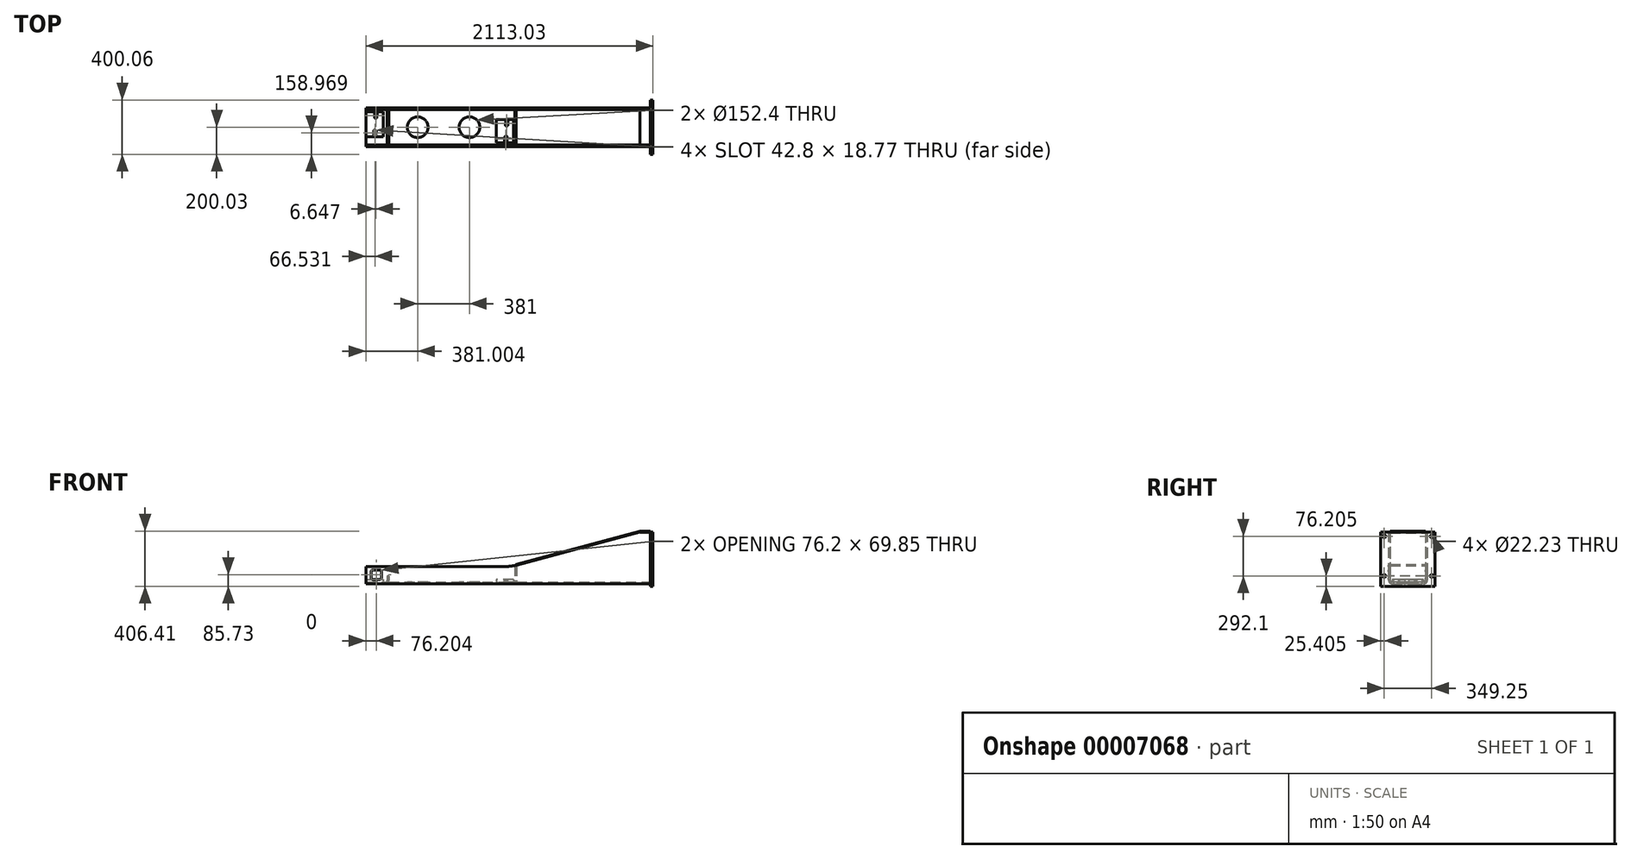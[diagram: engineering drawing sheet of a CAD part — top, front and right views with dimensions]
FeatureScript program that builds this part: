
annotation { "Feature Type Name" : "Feature", "Feature Type Description" : "" }
export const myFeature = defineFeature(function(context is Context, id is Id, definition is map)
    precondition{}
    {
        {
            var Q0;
            Q0=qCreatedBy(makeId("Right.planeOp"),FACE);
            var sketch = newSketch(context, id + "F0", { "sketchPlane" : qUnion([Q0])});
            skLineSegment(sketch, "E0.rect.bottom", {"start": v(-200.02, 200.03) * mm, "end": v(200.03, 200.03) * mm});
            skLineSegment(sketch, "E0.rect.top", {"start": v(-200.03, -200.03) * mm, "end": v(200.02, -200.03) * mm});
            skLineSegment(sketch, "E0.rect.left", {"start": v(-200.02, 200.03) * mm, "end": v(-200.03, -200.03) * mm});
            skLineSegment(sketch, "E0.rect.right", {"start": v(200.03, 200.03) * mm, "end": v(200.02, -200.03) * mm});
            skPoint(sketch, "E0.rect.middle", {"position": v(0, 0) * mm});
            skLineSegment(sketch, "E1.0", {"start": v(-200.03, -123.83) * mm, "end": v(200.02, -123.83) * mm, "construction": true});
            skLineSegment(sketch, "E2.0", {"start": v(-200.03, 168.28) * mm, "end": v(200.02, 168.28) * mm, "construction": true});
            skLineSegment(sketch, "E3", {"start": v(0, 200.03) * mm, "end": v(0, -200.03) * mm, "construction": true});
            skLineSegment(sketch, "E4.0", {"start": v(-174.62, 200.03) * mm, "end": v(-174.63, -200.02) * mm, "construction": true});
            skCircle(sketch, "E5", {"center": v(-174.62, 168.28) * mm, "radius": 11.11 * mm});
            skCircle(sketch, "E6", {"center": v(-174.63, -123.83) * mm, "radius": 11.11 * mm});
            skCircle(sketch, "E7.0.MirrorC", {"center": v(174.63, 168.27) * mm, "radius": 11.11 * mm});
            skCircle(sketch, "E8.0.MirrorC", {"center": v(174.62, -123.83) * mm, "radius": 11.11 * mm});
            skSolve(sketch);
        }
        {
            var Q0;
            Q0 = qSketchRegion(id + "F0", true);
            extrude(context, id + "F1", {"entities" : qUnion([Q0]), "depth" : 19.05 * mm});
        }
        {
            var Q0;
            Q0=makeQuery(id+"F1.opExtrude","CAP_FACE",FACE,{"disambiguationData":[OSD([sQuery(id+"F0.wireOp",EDGE,"E0.rect.bottom"),sQuery(id+"F0.wireOp",EDGE,"E0.rect.top"),sQuery(id+"F0.wireOp",EDGE,"E0.rect.left"),sQuery(id+"F0.wireOp",EDGE,"E0.rect.right"),sQuery(id+"F0.wireOp",EDGE,"E5"),sQuery(id+"F0.wireOp",EDGE,"E6"),sQuery(id+"F0.wireOp",EDGE,"E7.0.MirrorC"),sQuery(id+"F0.wireOp",EDGE,"E8.0.MirrorC")])],"isStart":true});
            var sketch = newSketch(context, id + "F2", { "sketchPlane" : qUnion([Q0])});
            skLineSegment(sketch, "E9", {"start": v(0, 200.03) * mm, "end": v(0, -200.03) * mm, "construction": true});
            skLineSegment(sketch, "E10.0", {"start": v(0, -180.97) * mm, "end": v(-117.47, -180.97) * mm});
            skLineSegment(sketch, "E11.0", {"start": v(0, -168.28) * mm, "end": v(-117.47, -168.28) * mm});
            skLineSegment(sketch, "E12.0", {"start": v(-130.18, 200.02) * mm, "end": v(-130.17, -155.58) * mm});
            skLineSegment(sketch, "E13.0", {"start": v(-142.88, 200.02) * mm, "end": v(-142.87, -155.57) * mm});
            skArc(sketch, "E14.filletArc", {"start": v(-130.17, -155.58) * mm, "mid": v(-126.46, -164.56) * mm, "end": v(-117.47, -168.28) * mm});
            skArc(sketch, "E15.filletArc", {"start": v(-142.87, -155.57) * mm, "mid": v(-135.44, -173.54) * mm, "end": v(-117.47, -180.97) * mm});
            skLineSegment(sketch, "E16", {"start": v(-142.88, 200.02) * mm, "end": v(-130.18, 200.02) * mm});
            skLineSegment(sketch, "E17.0.MirrorCS", {"start": v(142.87, 200.03) * mm, "end": v(130.17, 200.03) * mm});
            skArc(sketch, "E17.1.MirrorCS", {"start": v(130.18, -155.57) * mm, "mid": v(126.46, -164.56) * mm, "end": v(117.48, -168.27) * mm});
            skLineSegment(sketch, "E17.2.MirrorCS", {"start": v(0, -180.97) * mm, "end": v(117.48, -180.97) * mm});
            skLineSegment(sketch, "E17.3.MirrorCS", {"start": v(130.17, 200.03) * mm, "end": v(130.18, -155.57) * mm});
            skLineSegment(sketch, "E17.4.MirrorCS", {"start": v(0, -168.28) * mm, "end": v(117.48, -168.27) * mm});
            skLineSegment(sketch, "E17.5.MirrorCS", {"start": v(142.87, 200.03) * mm, "end": v(142.88, -155.57) * mm});
            skArc(sketch, "E17.6.MirrorCS", {"start": v(142.88, -155.57) * mm, "mid": v(135.44, -173.54) * mm, "end": v(117.48, -180.97) * mm});
            skSolve(sketch);
        }
        {
            var Q0;
            Q0 = qSketchRegion(id + "F2", true);
            extrude(context, id + "F3", {"entities" : qUnion([Q0]), "operationType" : NewBodyOperationType.ADD, "depth" : 2093.98 * mm});
        }
        {
            var Q0;
            Q0=makeQuery(id+"F3.opExtrude","SWEPT_FACE",FACE,{"disambiguationData":[OSD([sQuery(id+"F2.wireOp",EDGE,"E17.5.MirrorCS")])]});
            var sketch = newSketch(context, id + "F4", { "sketchPlane" : qUnion([Q0])});
            skLineSegment(sketch, "E18.0", {"start": v(-76.2, 200.02) * mm, "end": v(-76.2, -200.03) * mm, "construction": true});
            skLineSegment(sketch, "E19.0", {"start": v(-2093.98, -53.97) * mm, "end": v(-1064.27, -53.97) * mm});
            skLineSegment(sketch, "E20", {"start": v(-76.2, 200.02) * mm, "end": v(-985.38, -43.59) * mm});
            skLineSegment(sketch, "E21", {"start": v(-89.08, 249.31) * mm, "end": v(-1474.33, 249.31) * mm, "construction": true});
            skArc(sketch, "E22.filletArc", {"start": v(-1064.27, -53.97) * mm, "mid": v(-1024.48, -51.37) * mm, "end": v(-985.38, -43.59) * mm});
            skLineSegment(sketch, "E23", {"start": v(-76.2, 200.02) * mm, "end": v(-76.2, 325.81) * mm});
            skLineSegment(sketch, "E24", {"start": v(-76.2, 325.81) * mm, "end": v(-2093.98, 325.81) * mm});
            skLineSegment(sketch, "E25", {"start": v(-2093.98, 325.81) * mm, "end": v(-2093.98, -53.97) * mm});
            skSolve(sketch);
        }
        {
            var Q0;
            Q0 = qSketchRegion(id + "F4", true);
            extrude(context, id + "F5", {"entities" : qUnion([Q0]), "operationType" : NewBodyOperationType.REMOVE, "endBound" : BoundingType.THROUGH_ALL, "oppositeDirection" : true, "depth" : 25.4 * mm});
        }
        {
            var Q0;
            Q0=makeQuery(id+"F3.opExtrude","SWEPT_FACE",FACE,{"disambiguationData":[OSD([sQuery(id+"F2.wireOp",EDGE,"E12.0")])]});
            var sketch = newSketch(context, id + "F6", { "sketchPlane" : qUnion([Q0])});
            skLineSegment(sketch, "E26.0", {"start": v(-76.25, 200.21) * mm, "end": v(-985.43, -43.4) * mm});
            skSolve(sketch);
        }
        {
            var Q0;
            {var subQ0=sQuery(id+"F2.wireOp",EDGE,"E12.0");Q0=makeQuery(id+"F6.imprint","IMPRINT",FACE,{"disambiguationData":[TD([[makeQuery(id+"F6.imprint","IMPRINT",EDGE,{"derivedFrom":makeQuery(id+"F3.opExtrude","CAP_EDGE",EDGE,{"disambiguationData":[OSD([subQ0])],"isStart":true})}),-1.0]])]});}
            var sketch = newSketch(context, id + "F7", { "sketchPlane" : qUnion([Q0])});
            skLineSegment(sketch, "E27.0", {"start": v(-74.6, 194.08) * mm, "end": v(-983.79, -49.53) * mm});
            skLineSegment(sketch, "E28.0", {"start": v(-77.9, 206.35) * mm, "end": v(-987.07, -37.27) * mm});
            skLineSegment(sketch, "E29.0", {"start": v(-76.2, 193.68) * mm, "end": v(0, 193.68) * mm});
            skLineSegment(sketch, "E30.0", {"start": v(-76.2, 206.38) * mm, "end": v(0, 206.38) * mm});
            skLineSegment(sketch, "E31", {"start": v(-76.2, 206.38) * mm, "end": v(-76.2, 193.68) * mm});
            skLineSegment(sketch, "E32", {"start": v(-74.6, 194.08) * mm, "end": v(-77.9, 206.35) * mm});
            skLineSegment(sketch, "E33", {"start": v(0, 206.38) * mm, "end": v(0, 193.68) * mm});
            skLineSegment(sketch, "E34", {"start": v(-987.07, -37.27) * mm, "end": v(-983.79, -49.53) * mm});
            skSolve(sketch);
        }
        {
            var Q0;
            Q0 = qSketchRegion(id + "F7", true);
            extrude(context, id + "F8", {"entities" : qUnion([Q0]), "operationType" : NewBodyOperationType.ADD, "depth" : 260.35 * mm});
        }
        {
            var Q0;
            Q0=qCreatedBy(makeId("Right.planeOp"),FACE);
            cPlane(context, id + "F9", {"entities" : qUnion([Q0]), "cplaneType" : CPlaneType.OFFSET, "offset" : 984.25 * mm, "oppositeDirection" : true, "width" : 152.4 * mm, "height" : 152.4 * mm});
        }
        {
            var Q0;
            Q0=qCreatedBy(id+"F9.planeOp",FACE);
            var sketch = newSketch(context, id + "F10", { "sketchPlane" : qUnion([Q0])});
            skLineSegment(sketch, "E35.0", {"start": v(-130.18, -49.53) * mm, "end": v(130.17, -49.53) * mm});
            skLineSegment(sketch, "E36.0", {"start": v(130.17, -49.53) * mm, "end": v(130.17, -155.58) * mm});
            skArc(sketch, "E37.0", {"start": v(130.17, -155.58) * mm, "mid": v(126.46, -164.56) * mm, "end": v(117.47, -168.28) * mm});
            skLineSegment(sketch, "E38.0", {"start": v(117.47, -168.28) * mm, "end": v(-117.48, -168.27) * mm});
            skArc(sketch, "E39.0", {"start": v(-130.18, -155.57) * mm, "mid": v(-126.46, -164.56) * mm, "end": v(-117.48, -168.27) * mm});
            skLineSegment(sketch, "E40.0", {"start": v(-130.18, -49.53) * mm, "end": v(-130.18, -155.57) * mm});
            skPoint(sketch, "E41.orphan", {"position": v(130.17, -53.97) * mm});
            skPoint(sketch, "E42.orphan", {"position": v(-130.18, -53.97) * mm});
            skSolve(sketch);
        }
        {
            var Q0;
            Q0 = qSketchRegion(id + "F10", true);
            extrude(context, id + "F11", {"entities" : qUnion([Q0]), "operationType" : NewBodyOperationType.ADD, "oppositeDirection" : true, "depth" : 12.7 * mm});
        }
        {
            var Q0;
            {var subQ0=sQuery(id+"F2.wireOp",EDGE,"E11.0");var subQ1=sQuery(id+"F2.wireOp",EDGE,"E17.4.MirrorCS");Q0=makeQuery(id+"F11.boolean.opBoolean","SPLIT",FACE,{"disambiguationData":[TD([makeQuery(id+"F11.opExtrude","CAP_FACE",FACE,{"disambiguationData":[OSD([sQuery(id+"F10.wireOp",EDGE,"E35.0"),sQuery(id+"F10.wireOp",EDGE,"E36.0"),sQuery(id+"F10.wireOp",EDGE,"E37.0"),sQuery(id+"F10.wireOp",EDGE,"E38.0"),sQuery(id+"F10.wireOp",EDGE,"E39.0"),sQuery(id+"F10.wireOp",EDGE,"E40.0")])],"isStart":false})])],"derivedFrom":makeQuery(id+"F3.opExtrude","SWEPT_FACE",FACE,{"disambiguationData":[OSD([subQ0,subQ1])]})});}
            var sketch = newSketch(context, id + "F12", { "sketchPlane" : qUnion([Q0])});
            skLineSegment(sketch, "E43.0", {"start": v(-2093.98, 117.47) * mm, "end": v(-2093.98, -117.48) * mm, "construction": true});
            skLineSegment(sketch, "E44", {"start": v(-2093.98, 0) * mm, "end": v(-1025.05, 0) * mm, "construction": true});
            skLineSegment(sketch, "E45.0", {"start": v(-1712.98, 117.47) * mm, "end": v(-1712.98, -117.48) * mm, "construction": true});
            skLineSegment(sketch, "E46.0", {"start": v(-1331.98, 117.47) * mm, "end": v(-1331.98, -117.48) * mm, "construction": true});
            skCircle(sketch, "E47", {"center": v(-1712.98, 0) * mm, "radius": 76.2 * mm});
            skCircle(sketch, "E48", {"center": v(-1331.98, 0) * mm, "radius": 76.2 * mm});
            skSolve(sketch);
        }
        {
            var Q0;
            Q0 = qSketchRegion(id + "F12", true);
            extrude(context, id + "F13", {"entities" : qUnion([Q0]), "operationType" : NewBodyOperationType.REMOVE, "endBound" : BoundingType.THROUGH_ALL, "oppositeDirection" : true, "depth" : 25.4 * mm});
        }
        {
            var Q0;
            Q0=makeQuery(id+"F3.opExtrude","SWEPT_FACE",FACE,{"disambiguationData":[OSD([sQuery(id+"F2.wireOp",EDGE,"E17.5.MirrorCS")])]});
            var sketch = newSketch(context, id + "F14", { "sketchPlane" : qUnion([Q0])});
            skLineSegment(sketch, "E49.0", {"start": v(-2043.18, -149.22) * mm, "end": v(-1992.38, -149.22) * mm});
            skLineSegment(sketch, "E50.0", {"start": v(-2043.18, -79.37) * mm, "end": v(-1992.38, -79.37) * mm});
            skLineSegment(sketch, "E51.0", {"start": v(-2055.88, -92.07) * mm, "end": v(-2055.88, -136.53) * mm});
            skLineSegment(sketch, "E52.0", {"start": v(-1979.68, -92.07) * mm, "end": v(-1979.68, -136.52) * mm});
            skPoint(sketch, "E53.visualSharp", {"position": v(-2055.88, -79.37) * mm});
            skArc(sketch, "E53.filletArc", {"start": v(-2043.18, -79.37) * mm, "mid": v(-2052.16, -83.1) * mm, "end": v(-2055.88, -92.07) * mm});
            skPoint(sketch, "E54.visualSharp", {"position": v(-1979.68, -79.37) * mm});
            skArc(sketch, "E54.filletArc", {"start": v(-1979.68, -92.07) * mm, "mid": v(-1983.4, -83.1) * mm, "end": v(-1992.38, -79.37) * mm});
            skPoint(sketch, "E55.visualSharp", {"position": v(-1979.68, -149.22) * mm});
            skArc(sketch, "E55.filletArc", {"start": v(-1992.38, -149.22) * mm, "mid": v(-1983.4, -145.5) * mm, "end": v(-1979.68, -136.52) * mm});
            skPoint(sketch, "E56.visualSharp", {"position": v(-2055.88, -149.22) * mm});
            skArc(sketch, "E56.filletArc", {"start": v(-2055.88, -136.53) * mm, "mid": v(-2052.16, -145.5) * mm, "end": v(-2043.18, -149.23) * mm});
            skSolve(sketch);
        }
        {
            var Q0;
            Q0 = qSketchRegion(id + "F14", true);
            extrude(context, id + "F15", {"entities" : qUnion([Q0]), "operationType" : NewBodyOperationType.REMOVE, "endBound" : BoundingType.THROUGH_ALL, "oppositeDirection" : true, "depth" : 25.4 * mm});
        }
        {
            var Q0;
            Q0=makeQuery(id+"F11.opExtrude","CAP_FACE",FACE,{"disambiguationData":[OSD([sQuery(id+"F10.wireOp",EDGE,"E35.0"),sQuery(id+"F10.wireOp",EDGE,"E36.0"),sQuery(id+"F10.wireOp",EDGE,"E37.0"),sQuery(id+"F10.wireOp",EDGE,"E38.0"),sQuery(id+"F10.wireOp",EDGE,"E39.0"),sQuery(id+"F10.wireOp",EDGE,"E40.0")])],"isStart":false});
            cPlane(context, id + "F16", {"entities" : qUnion([Q0]), "cplaneType" : CPlaneType.OFFSET, "offset" : 939.8 * mm, "width" : 152.4 * mm, "height" : 152.4 * mm});
        }
        {
            var Q0;
            Q0=qCreatedBy(id+"F16.planeOp",FACE);
            var sketch = newSketch(context, id + "F17", { "sketchPlane" : qUnion([Q0])});
            skLineSegment(sketch, "E57.0", {"start": v(-130.17, -123.83) * mm, "end": v(-130.17, -155.58) * mm});
            skArc(sketch, "E58.0", {"start": v(-130.17, -155.58) * mm, "mid": v(-126.46, -164.56) * mm, "end": v(-117.47, -168.28) * mm});
            skLineSegment(sketch, "E59.0", {"start": v(-117.47, -168.28) * mm, "end": v(117.48, -168.27) * mm});
            skArc(sketch, "E60.0", {"start": v(130.18, -155.57) * mm, "mid": v(126.46, -164.56) * mm, "end": v(117.48, -168.27) * mm});
            skLineSegment(sketch, "E61.0", {"start": v(130.18, -123.82) * mm, "end": v(130.18, -155.57) * mm});
            skLineSegment(sketch, "E62.0", {"start": v(-130.17, -123.83) * mm, "end": v(130.18, -123.82) * mm});
            skPoint(sketch, "E63.orphan", {"position": v(-130.17, -53.97) * mm});
            skPoint(sketch, "E64.orphan", {"position": v(130.18, -53.97) * mm});
            skSolve(sketch);
        }
        {
            var Q0;
            Q0 = qSketchRegion(id + "F17", true);
            extrude(context, id + "F18", {"entities" : qUnion([Q0]), "operationType" : NewBodyOperationType.ADD, "oppositeDirection" : true, "depth" : 12.7 * mm});
        }
        {
            var Q0;
            {var subQ0=sQuery(id+"F2.wireOp",EDGE,"E11.0");var subQ1=sQuery(id+"F2.wireOp",EDGE,"E17.4.MirrorCS");Q0=makeQuery(id+"F18.boolean.opBoolean","SPLIT",FACE,{"disambiguationData":[TD([makeQuery(id+"F18.opExtrude","CAP_FACE",FACE,{"disambiguationData":[OSD([sQuery(id+"F17.wireOp",EDGE,"E57.0"),sQuery(id+"F17.wireOp",EDGE,"E58.0"),sQuery(id+"F17.wireOp",EDGE,"E59.0"),sQuery(id+"F17.wireOp",EDGE,"E60.0"),sQuery(id+"F17.wireOp",EDGE,"E61.0"),sQuery(id+"F17.wireOp",EDGE,"E62.0")])],"isStart":true})])],"derivedFrom":makeQuery(id+"F11.boolean.opBoolean","SPLIT",FACE,{"disambiguationData":[TD([makeQuery(id+"F11.opExtrude","CAP_FACE",FACE,{"disambiguationData":[OSD([sQuery(id+"F10.wireOp",EDGE,"E35.0"),sQuery(id+"F10.wireOp",EDGE,"E36.0"),sQuery(id+"F10.wireOp",EDGE,"E37.0"),sQuery(id+"F10.wireOp",EDGE,"E38.0"),sQuery(id+"F10.wireOp",EDGE,"E39.0"),sQuery(id+"F10.wireOp",EDGE,"E40.0")])],"isStart":false})])],"derivedFrom":makeQuery(id+"F3.opExtrude","SWEPT_FACE",FACE,{"disambiguationData":[OSD([subQ0,subQ1])]})})});}
            var sketch = newSketch(context, id + "F19", { "sketchPlane" : qUnion([Q0])});
            skLineSegment(sketch, "E65.0", {"start": v(-2093.98, 114.3) * mm, "end": v(-2093.98, -69.85) * mm});
            skLineSegment(sketch, "E66.0", {"start": v(-1966.98, 114.3) * mm, "end": v(-1966.98, -69.85) * mm});
            skLineSegment(sketch, "E67", {"start": v(-2093.98, 0) * mm, "end": v(-1966.98, 0) * mm, "construction": true});
            skLineSegment(sketch, "E68.0", {"start": v(-2093.98, -69.85) * mm, "end": v(-1966.98, -69.85) * mm});
            skLineSegment(sketch, "E69.0", {"start": v(-2093.98, 114.3) * mm, "end": v(-1966.98, 114.3) * mm});
            skPoint(sketch, "E70.orphan", {"position": v(-1966.98, 117.47) * mm});
            skPoint(sketch, "E71.orphan", {"position": v(-2093.98, 117.47) * mm});
            skPoint(sketch, "E72.orphan", {"position": v(-1966.98, -117.48) * mm});
            skPoint(sketch, "E73.orphan", {"position": v(-2093.98, -117.48) * mm});
            skSolve(sketch);
        }
        {
            var Q0;
            Q0 = qSketchRegion(id + "F19", true);
            extrude(context, id + "F20", {"entities" : qUnion([Q0]), "operationType" : NewBodyOperationType.ADD, "depth" : 19.05 * mm});
        }
        {
            var Q0;
            {var subQ0=sQuery(id+"F2.wireOp",EDGE,"E11.0");var subQ1=sQuery(id+"F2.wireOp",EDGE,"E17.4.MirrorCS");var subQ6=makeQuery(id+"F11.opExtrude","CAP_FACE",FACE,{"disambiguationData":[OSD([sQuery(id+"F10.wireOp",EDGE,"E35.0"),sQuery(id+"F10.wireOp",EDGE,"E36.0"),sQuery(id+"F10.wireOp",EDGE,"E37.0"),sQuery(id+"F10.wireOp",EDGE,"E38.0"),sQuery(id+"F10.wireOp",EDGE,"E39.0"),sQuery(id+"F10.wireOp",EDGE,"E40.0")])],"isStart":false});Q0=makeQuery(id+"F18.boolean.opBoolean","SPLIT",FACE,{"disambiguationData":[TD([makeQuery(id+"F13.boolean.opBoolean","COPY",FACE,{"derivedFrom":makeQuery(id+"F13.opExtrude","SWEPT_FACE",FACE,{"disambiguationData":[OSD([sQuery(id+"F12.wireOp",EDGE,"E47")])]})})])],"derivedFrom":makeQuery(id+"F11.boolean.opBoolean","SPLIT",FACE,{"disambiguationData":[TD([subQ6])],"derivedFrom":makeQuery(id+"F3.opExtrude","SWEPT_FACE",FACE,{"disambiguationData":[OSD([subQ0,subQ1])]})})});}
            var sketch = newSketch(context, id + "F21", { "sketchPlane" : qUnion([Q0])});
            skLineSegment(sketch, "E74", {"start": v(-996.95, 0) * mm, "end": v(-2205.84, 0) * mm, "construction": true});
            skLineSegment(sketch, "E75.0", {"start": v(-1135.13, 57.15) * mm, "end": v(-1135.13, -114.3) * mm});
            skLineSegment(sketch, "E76.0", {"start": v(-1008.13, 57.15) * mm, "end": v(-1008.13, -114.3) * mm});
            skLineSegment(sketch, "E77.0", {"start": v(-1008.13, -114.3) * mm, "end": v(-1135.13, -114.3) * mm});
            skLineSegment(sketch, "E78.0", {"start": v(-1008.13, 57.15) * mm, "end": v(-1135.13, 57.15) * mm});
            skSolve(sketch);
        }
        {
            var Q0;
            Q0 = qSketchRegion(id + "F21", true);
            extrude(context, id + "F22", {"entities" : qUnion([Q0]), "operationType" : NewBodyOperationType.ADD, "depth" : 19.05 * mm});
        }
        {
            var Q0;
            Q0=makeQuery(id+"F22.opExtrude","CAP_FACE",FACE,{"disambiguationData":[OSD([sQuery(id+"F21.wireOp",EDGE,"E75.0"),sQuery(id+"F21.wireOp",EDGE,"E76.0"),sQuery(id+"F21.wireOp",EDGE,"E77.0"),sQuery(id+"F21.wireOp",EDGE,"E78.0")])],"isStart":false});
            var sketch = newSketch(context, id + "F23", { "sketchPlane" : qUnion([Q0])});
            skLineSegment(sketch, "E79", {"start": v(110.37, 0) * mm, "end": v(-2176.16, 0) * mm, "construction": true});
            skLineSegment(sketch, "E80.0", {"start": v(110.37, 22.35) * mm, "end": v(-2176.16, 22.35) * mm, "construction": true});
            skLineSegment(sketch, "E81.0", {"start": v(110.37, -28.45) * mm, "end": v(-2176.16, -28.45) * mm, "construction": true});
            skLineSegment(sketch, "E82.0", {"start": v(-2093.98, 114.3) * mm, "end": v(-2093.98, -69.85) * mm, "construction": true});
            skLineSegment(sketch, "E83.0", {"start": v(-2024.13, 114.3) * mm, "end": v(-2024.13, -69.85) * mm, "construction": true});
            skLineSegment(sketch, "E84.0", {"start": v(-1060.45, 114.3) * mm, "end": v(-1060.45, -69.85) * mm, "construction": true});
            skLineSegment(sketch, "E85", {"start": v(-2026.79, -28.45) * mm, "end": v(-2013.86, 218.3) * mm, "construction": true});
            skLineSegment(sketch, "E86", {"start": v(-2024.13, 22.35) * mm, "end": v(-1060.45, -28.15) * mm, "construction": true});
            skLineSegment(sketch, "E87.0", {"start": v(-2020.8, 85.76) * mm, "end": v(-1880.93, 78.43) * mm, "construction": true});
            skLineSegment(sketch, "E88.0", {"start": v(-2021.47, 73.08) * mm, "end": v(-1881.6, 65.75) * mm, "construction": true});
            skLineSegment(sketch, "E89", {"start": v(-2028.86, 98.9) * mm, "end": v(-2030.19, 73.54) * mm});
            skLineSegment(sketch, "E90", {"start": v(-2011.42, 98) * mm, "end": v(-2012.75, 72.63) * mm});
            skArc(sketch, "E91.trimOffspring", {"start": v(-2028.86, 98.9) * mm, "mid": v(-2019.68, 107.17) * mm, "end": v(-2011.42, 98) * mm});
            skArc(sketch, "E92.trimOffspring", {"start": v(-2030.19, 73.54) * mm, "mid": v(-2021.92, 64.36) * mm, "end": v(-2012.75, 72.63) * mm});
            skLineSegment(sketch, "E93.0.MirrorCS", {"start": v(-2019.4, -54.2) * mm, "end": v(-2018.07, -28.84) * mm});
            skArc(sketch, "E94.0.MirrorCS", {"start": v(-2036.83, -53.29) * mm, "mid": v(-2028.57, -62.46) * mm, "end": v(-2019.4, -54.2) * mm});
            skLineSegment(sketch, "E95.0.MirrorCS", {"start": v(-2036.83, -53.29) * mm, "end": v(-2035.5, -27.92) * mm});
            skArc(sketch, "E96.0.MirrorCS", {"start": v(-2035.5, -27.92) * mm, "mid": v(-2026.33, -19.66) * mm, "end": v(-2018.07, -28.84) * mm});
            skLineSegment(sketch, "E97", {"start": v(-1542.29, -2.9) * mm, "end": v(-1531.97, 193.95) * mm, "construction": true});
            skLineSegment(sketch, "E98.0.MirrorCS", {"start": v(-1063.11, -78.95) * mm, "end": v(-1050.18, 167.8) * mm, "construction": true});
            skLineSegment(sketch, "E99.0", {"start": v(-2027.12, -34.72) * mm, "end": v(-1063.44, -85.22) * mm, "construction": true});
            skLineSegment(sketch, "E100.0", {"start": v(-2026.45, -22.04) * mm, "end": v(-1062.78, -72.54) * mm, "construction": true});
            skArc(sketch, "E101", {"start": v(-1054.06, -73) * mm, "mid": v(-1062.32, -63.82) * mm, "end": v(-1071.5, -72.08) * mm});
            skArc(sketch, "E102.0.MirrorC", {"start": v(-1055.39, -98.36) * mm, "mid": v(-1064.56, -106.63) * mm, "end": v(-1072.82, -97.45) * mm});
            skLineSegment(sketch, "E103", {"start": v(-1071.5, -72.08) * mm, "end": v(-1072.82, -97.45) * mm});
            skLineSegment(sketch, "E104", {"start": v(-1054.06, -73) * mm, "end": v(-1055.39, -98.36) * mm});
            skLineSegment(sketch, "E105.0.MirrorCS", {"start": v(-1049.4, 15.78) * mm, "end": v(-1048.08, 41.15) * mm});
            skLineSegment(sketch, "E105.1.MirrorCS", {"start": v(-1066.84, 16.7) * mm, "end": v(-1065.51, 42.06) * mm});
            skArc(sketch, "E105.2.MirrorCS", {"start": v(-1048.08, 41.15) * mm, "mid": v(-1056.34, 50.32) * mm, "end": v(-1065.51, 42.06) * mm});
            skArc(sketch, "E105.3.MirrorCS", {"start": v(-1049.4, 15.78) * mm, "mid": v(-1058.58, 7.52) * mm, "end": v(-1066.84, 16.7) * mm});
            skSolve(sketch);
        }
        {
            var Q0;
            Q0 = qSketchRegion(id + "F23", true);
            extrude(context, id + "F24", {"entities" : qUnion([Q0]), "operationType" : NewBodyOperationType.REMOVE, "endBound" : BoundingType.THROUGH_ALL, "oppositeDirection" : true, "depth" : 25.4 * mm});
        }
    });
